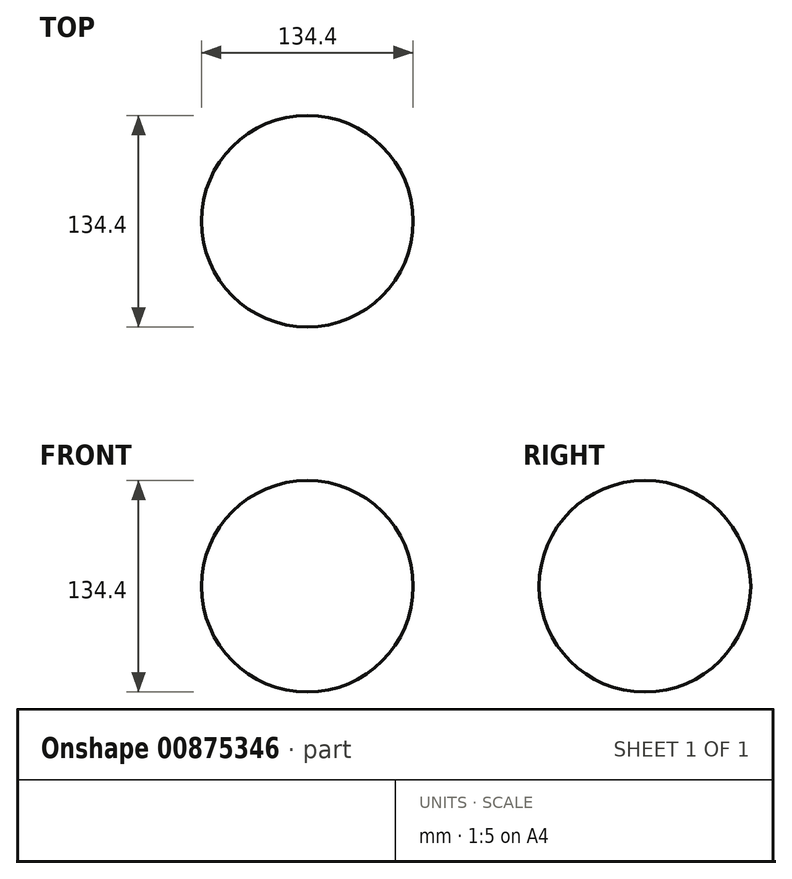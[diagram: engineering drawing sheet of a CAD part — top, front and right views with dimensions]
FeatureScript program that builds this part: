
annotation { "Feature Type Name" : "Feature", "Feature Type Description" : "" }
export const myFeature = defineFeature(function(context is Context, id is Id, definition is map)
    precondition{}
    {
        {
            var Q0;
            Q0=qCreatedBy(makeId("Front.planeOp"),FACE);
            var sketch = newSketch(context, id + "F0", { "sketchPlane" : qUnion([Q0])});
            skCircle(sketch, "E0", {"center": v(0, 0) * mm, "radius": 67.2 * mm});
            skLineSegment(sketch, "E1", {"start": v(0, 67.2) * mm, "end": v(0, -67.2) * mm});
            skSolve(sketch);
        }
        {
            var Q0;
            {var subQ0=sQuery(id+"F0.wireOp",EDGE,"E1");Q0=makeQuery(id+"F0.imprint","IMPRINT",FACE,{"disambiguationData":[TD([[makeQuery(id+"F0.imprint","IMPRINT",EDGE,{"derivedFrom":subQ0}),-1.0]])]});}
            var Q1;
            Q1=sQuery(id+"F0.wireOp",EDGE,"E1");
            revolve(context, id + "F1", {"surfaceOperationType" : NewSurfaceOperationType.NEW, "entities" : qUnion([Q0]), "axis" : qUnion([Q1]), "revolveType" : RevolveType.FULL});
        }
    });
